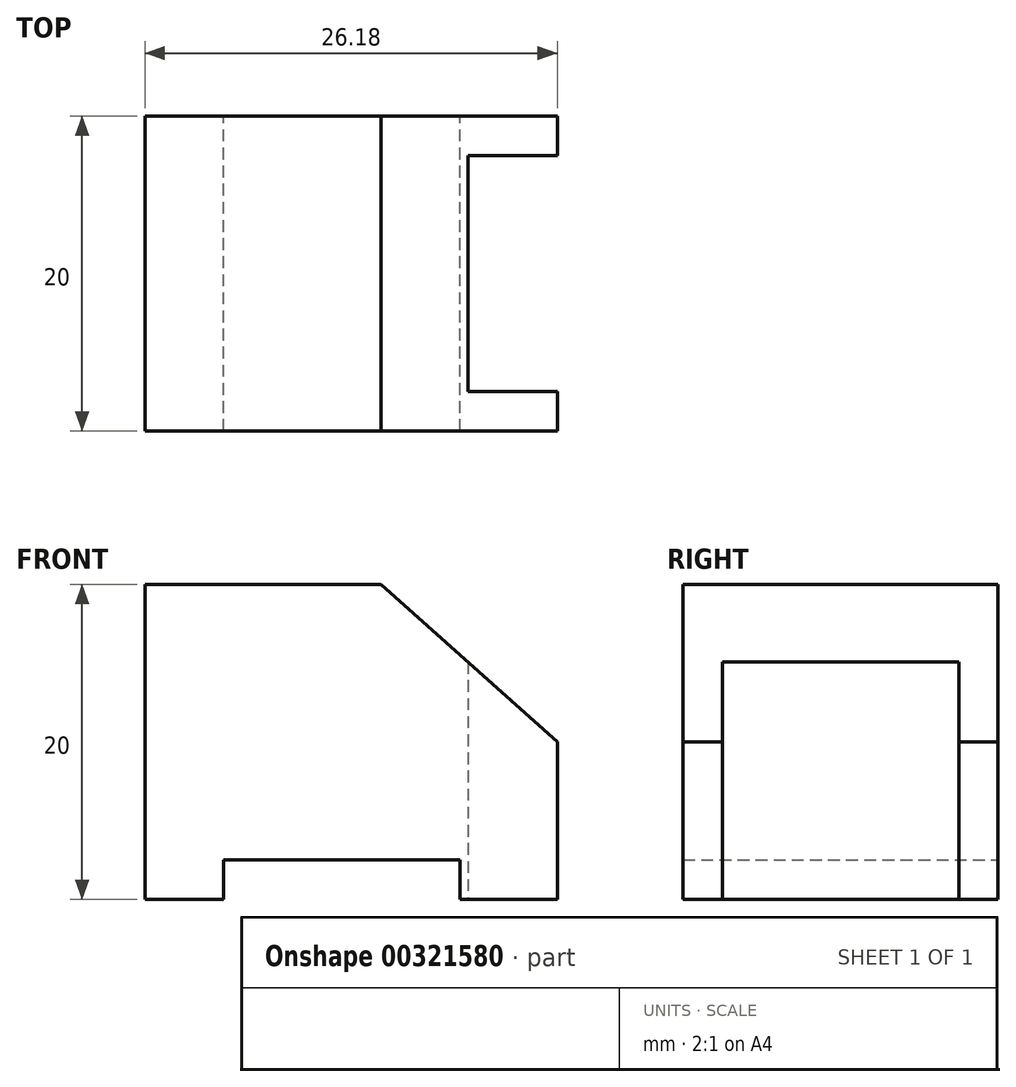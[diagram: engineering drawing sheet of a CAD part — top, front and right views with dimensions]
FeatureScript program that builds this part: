
annotation { "Feature Type Name" : "Feature", "Feature Type Description" : "" }
export const myFeature = defineFeature(function(context is Context, id is Id, definition is map)
    precondition{}
    {
        {
            var Q0;
            Q0=qCreatedBy(makeId("Front.planeOp"),FACE);
            var sketch = newSketch(context, id + "F0", { "sketchPlane" : qUnion([Q0])});
            skLineSegment(sketch, "E0", {"start": v(0, 0) * mm, "end": v(0, 20) * mm});
            skLineSegment(sketch, "E1", {"start": v(0, 20) * mm, "end": v(15, 20) * mm});
            skLineSegment(sketch, "E2", {"start": v(15, 20) * mm, "end": v(26.18, 10) * mm});
            skLineSegment(sketch, "E3", {"start": v(26.18, 10) * mm, "end": v(26.18, 0) * mm});
            skLineSegment(sketch, "E4", {"start": v(26.18, 0) * mm, "end": v(20, 0) * mm});
            skLineSegment(sketch, "E5", {"start": v(20, 0) * mm, "end": v(20, 2.5) * mm});
            skLineSegment(sketch, "E6", {"start": v(20, 2.5) * mm, "end": v(5, 2.5) * mm});
            skLineSegment(sketch, "E7", {"start": v(5, 2.5) * mm, "end": v(5, 0) * mm});
            skLineSegment(sketch, "E8", {"start": v(5, 0) * mm, "end": v(0, 0) * mm});
            skSolve(sketch);
        }
        {
            var Q0;
            Q0 = qSketchRegion(id + "F0", true);
            extrude(context, id + "F1", {"entities" : qUnion([Q0]), "depth" : 20 * mm});
        }
        {
            var Q0;
            Q0=qCreatedBy(makeId("Top.planeOp"),FACE);
            var sketch = newSketch(context, id + "F2", { "sketchPlane" : qUnion([Q0])});
            skLineSegment(sketch, "E9", {"start": v(26.18, -2.5) * mm, "end": v(20.5, -2.5) * mm});
            skLineSegment(sketch, "E10", {"start": v(20.5, -2.5) * mm, "end": v(20.5, -17.5) * mm});
            skLineSegment(sketch, "E11", {"start": v(20.5, -17.5) * mm, "end": v(26.18, -17.5) * mm});
            skLineSegment(sketch, "E12", {"start": v(26.18, -2.5) * mm, "end": v(26.18, -17.5) * mm});
            skSolve(sketch);
        }
        {
            var Q0;
            Q0 = qSketchRegion(id + "F2", true);
            extrude(context, id + "F3", {"entities" : qUnion([Q0]), "operationType" : NewBodyOperationType.REMOVE, "endBound" : BoundingType.THROUGH_ALL, "depth" : 20 * mm});
        }
    });
